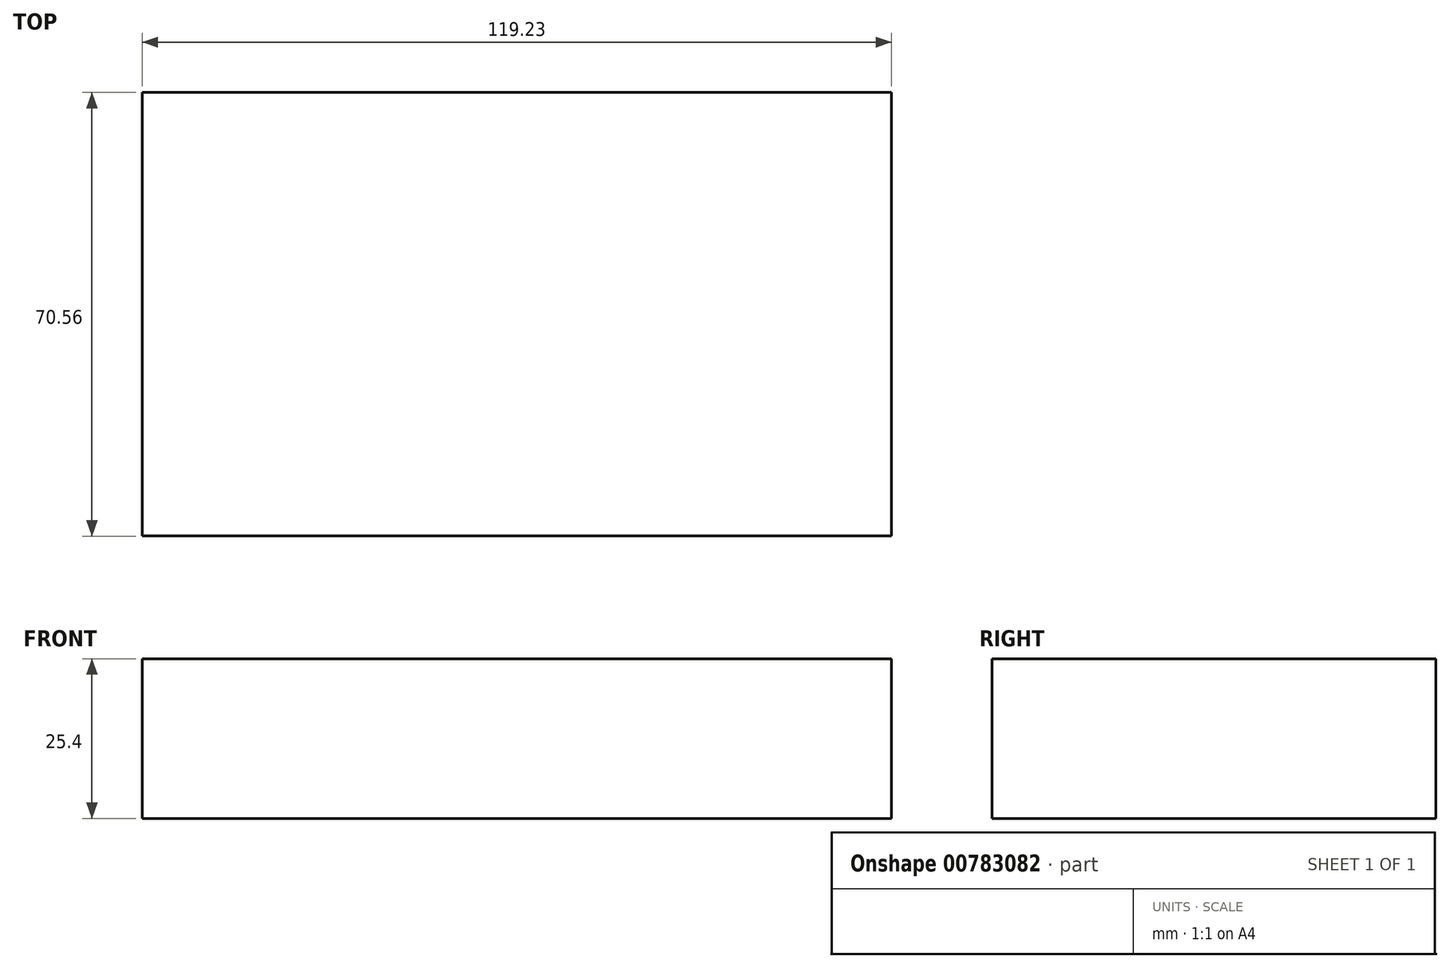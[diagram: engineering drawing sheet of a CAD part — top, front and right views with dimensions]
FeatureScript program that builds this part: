
annotation { "Feature Type Name" : "Feature", "Feature Type Description" : "" }
export const myFeature = defineFeature(function(context is Context, id is Id, definition is map)
    precondition{}
    {
        {
            var Q0;
            Q0=qCreatedBy(makeId("Top.planeOp"),FACE);
            var sketch = newSketch(context, id + "F0", { "sketchPlane" : qUnion([Q0])});
            skLineSegment(sketch, "E0.bottom", {"start": v(-57.79, 26) * mm, "end": v(61.44, 26) * mm});
            skLineSegment(sketch, "E0.top", {"start": v(-57.79, -44.56) * mm, "end": v(61.44, -44.56) * mm});
            skLineSegment(sketch, "E0.left", {"start": v(-57.79, 26) * mm, "end": v(-57.79, -44.56) * mm});
            skLineSegment(sketch, "E0.right", {"start": v(61.44, 26) * mm, "end": v(61.44, -44.56) * mm});
            skSolve(sketch);
        }
        {
            var Q0;
            Q0=makeQuery(id+"F0.imprint","IMPRINT",FACE,{"disambiguationData":[TD([[makeQuery(id+"F0.imprint","IMPRINT",EDGE,{"derivedFrom":sQuery(id+"F0.wireOp",EDGE,"E0.bottom")}),-1.0]])]});
            extrude(context, id + "F1", {"entities" : qUnion([Q0]), "depth" : 25.4 * mm});
        }
    });
